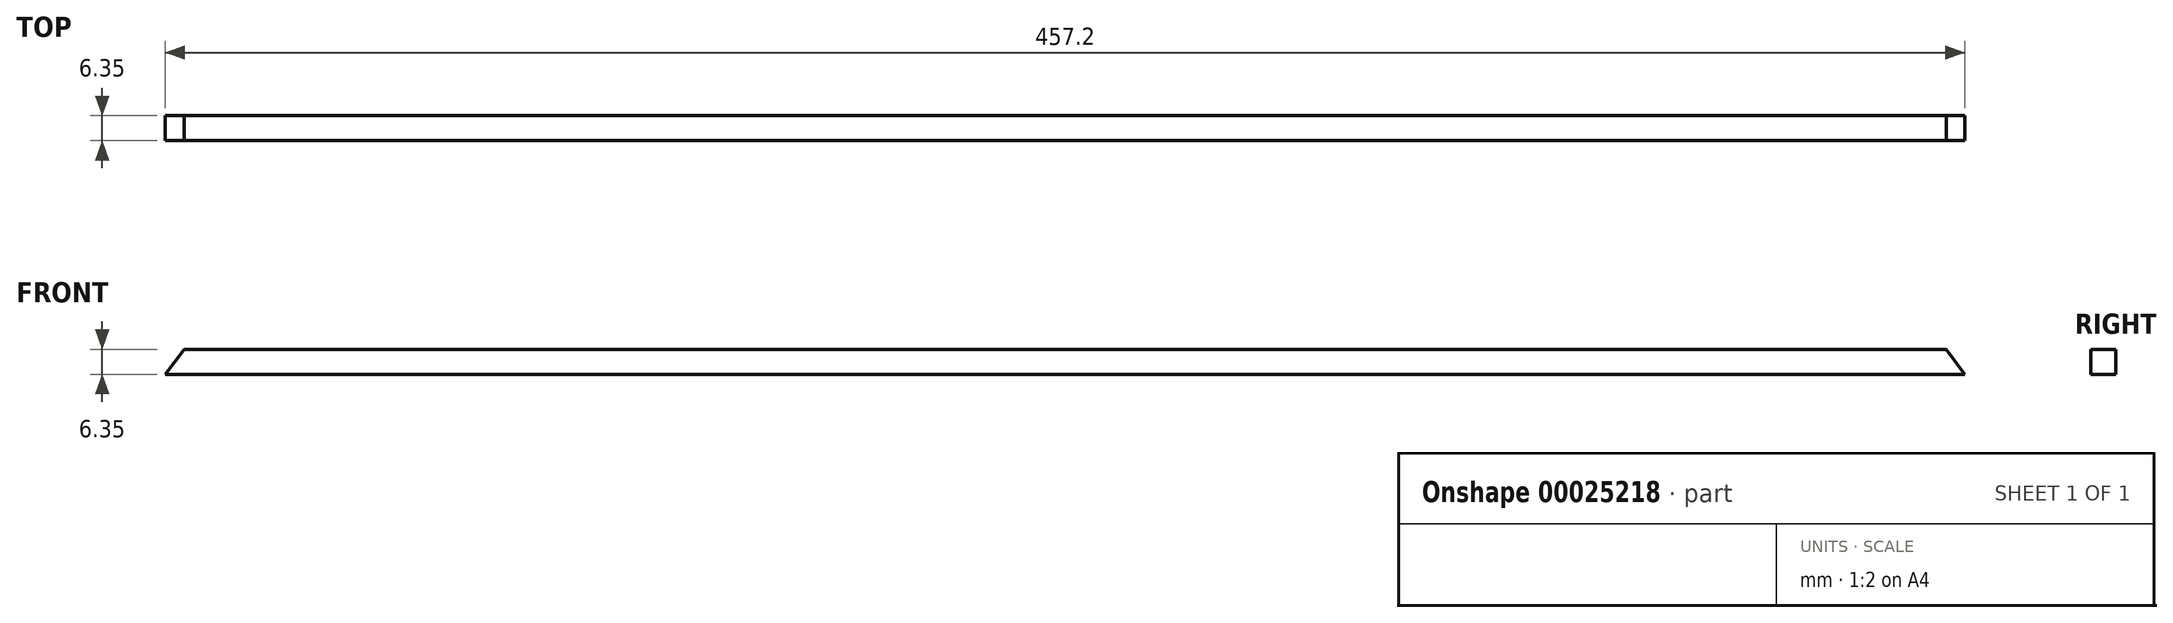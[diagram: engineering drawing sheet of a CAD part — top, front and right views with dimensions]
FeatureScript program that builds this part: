
annotation { "Feature Type Name" : "Feature", "Feature Type Description" : "" }
export const myFeature = defineFeature(function(context is Context, id is Id, definition is map)
    precondition{}
    {
        {
            var Q0;
            Q0=qCreatedBy(makeId("Front.planeOp"),FACE);
            var sketch = newSketch(context, id + "F0", { "sketchPlane" : qUnion([Q0])});
            skLineSegment(sketch, "E0", {"start": v(0, 0) * mm, "end": v(-4.76, 6.35) * mm});
            skLineSegment(sketch, "E1", {"start": v(-228.6, 6.35) * mm, "end": v(-4.76, 6.35) * mm});
            skLineSegment(sketch, "E2", {"start": v(0, 0) * mm, "end": v(-228.6, 0) * mm});
            skLineSegment(sketch, "E3.MirrorCS", {"start": v(-228.6, 6.35) * mm, "end": v(-452.44, 6.35) * mm});
            skLineSegment(sketch, "E4.MirrorCS", {"start": v(-457.2, 0) * mm, "end": v(-228.6, 0) * mm});
            skLineSegment(sketch, "E5.MirrorCS", {"start": v(-457.2, 0) * mm, "end": v(-452.44, 6.35) * mm});
            skSolve(sketch);
        }
        {
            var Q0;
            Q0 = qSketchRegion(id + "F0", true);
            extrude(context, id + "F1", {"entities" : qUnion([Q0]), "depth" : 6.35 * mm});
        }
    });
